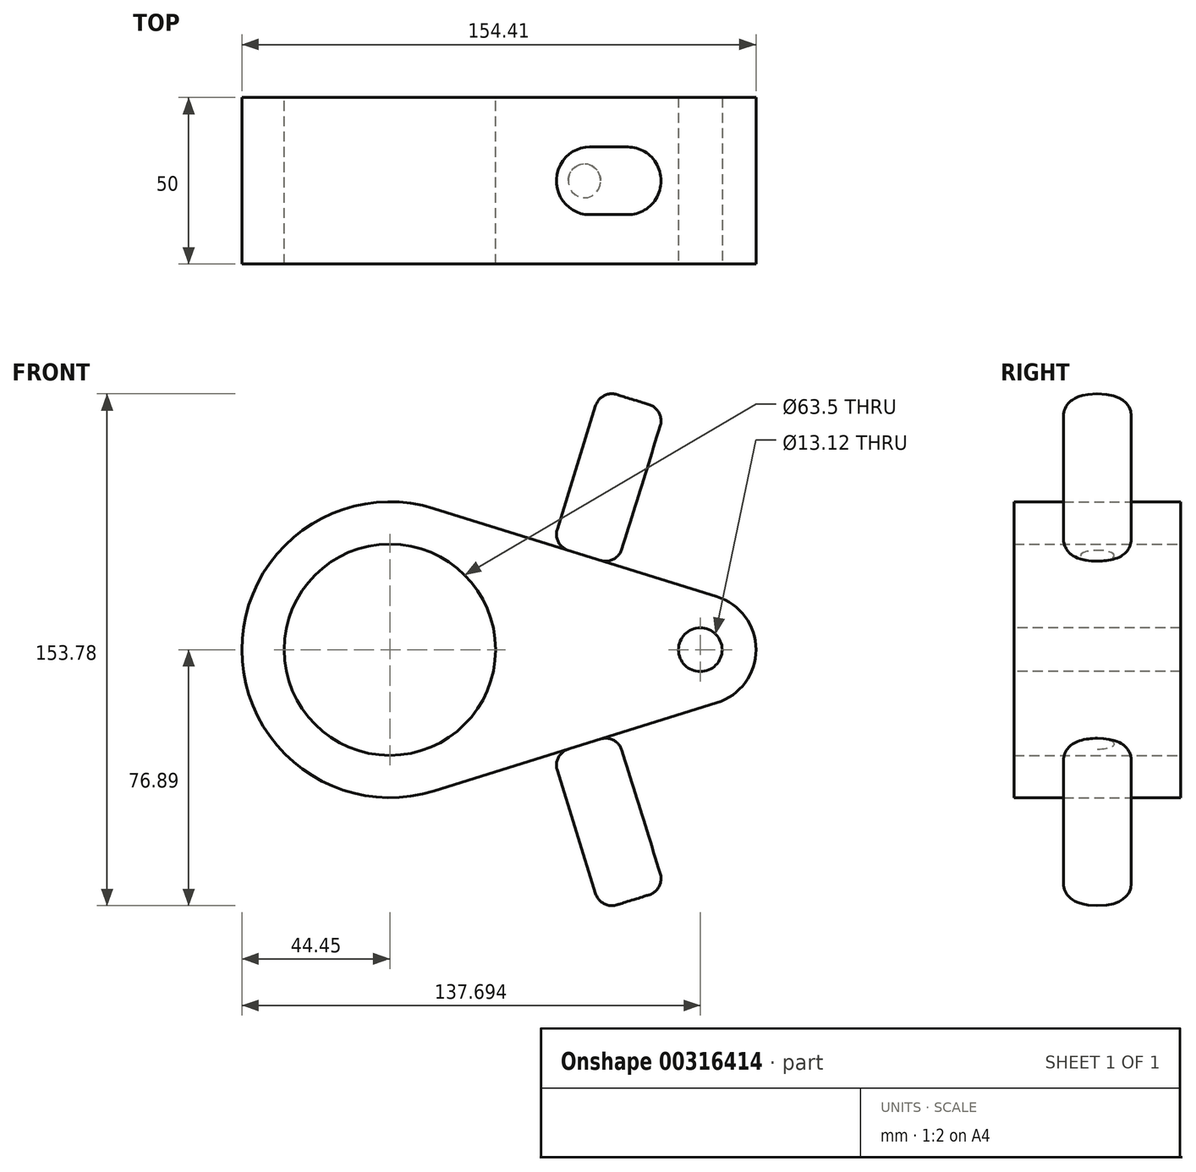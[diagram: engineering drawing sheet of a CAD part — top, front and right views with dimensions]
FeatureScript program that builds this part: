
annotation { "Feature Type Name" : "Feature", "Feature Type Description" : "" }
export const myFeature = defineFeature(function(context is Context, id is Id, definition is map)
    precondition{}
    {
        {
            var Q0;
            Q0=qCreatedBy(makeId("Front.planeOp"),FACE);
            var sketch = newSketch(context, id + "F0", { "sketchPlane" : qUnion([Q0])});
            skCircle(sketch, "E0", {"center": v(0, 0) * mm, "radius": 44.45 * mm});
            skCircle(sketch, "E1", {"center": v(93.24, 0) * mm, "radius": 16.72 * mm});
            skLineSegment(sketch, "E2", {"start": v(13.22, 42.44) * mm, "end": v(98.22, 15.96) * mm});
            skLineSegment(sketch, "E3", {"start": v(13.22, -42.44) * mm, "end": v(98.22, -15.96) * mm});
            skCircle(sketch, "E4", {"center": v(0, 0) * mm, "radius": 31.75 * mm});
            skSolve(sketch);
        }
        {
            var Q0;
            Q0 = qSketchRegion(id + "F0", true);
            extrude(context, id + "F1", {"entities" : qUnion([Q0]), "depth" : 50 * mm});
        }
        {
            var Q0;
            Q0=makeQuery(id+"F1.opExtrude","SWEPT_FACE",FACE,{"disambiguationData":[OSD([sQuery(id+"F0.wireOp",EDGE,"E2")])]});
            var sketch = newSketch(context, id + "F2", { "sketchPlane" : qUnion([Q0])});
            skCircle(sketch, "E5", {"center": v(47.38, -25) * mm, "radius": 10.16 * mm});
            skPoint(sketch, "E5.centerSnap0", {"position": v(89.03, -25) * mm});
            skSolve(sketch);
        }
        {
            var Q0;
            Q0 = qSketchRegion(id + "F2", true);
            extrude(context, id + "F3", {"entities" : qUnion([Q0]), "depth" : 49.02 * mm});
        }
        {
            var Q0;
            Q0=makeQuery(id+"F3.opExtrude","CAP_EDGE",EDGE,{"disambiguationData":[OSD([sQuery(id+"F2.wireOp",EDGE,"E5")])],"isStart":false});
            var Q1;
            Q1=makeQuery(id+"F3.opExtrude","CAP_EDGE",EDGE,{"disambiguationData":[OSD([sQuery(id+"F2.wireOp",EDGE,"E5")])],"isStart":true});
            fillet(context, id + "F4", {"entities" : qUnion([Q0, Q1]), "radius" : 5.08 * mm, "tangentPropagation" : true, "allowEdgeOverflow" : false});
        }
        {
            var Q0;
            Q0=makeQuery(id+"F1.opExtrude","CAP_FACE",FACE,{"disambiguationData":[OSD([sQuery(id+"F0.wireOp",EDGE,"E0"),sQuery(id+"F0.wireOp",EDGE,"E1"),sQuery(id+"F0.wireOp",EDGE,"E2"),sQuery(id+"F0.wireOp",EDGE,"E3"),sQuery(id+"F0.wireOp",EDGE,"E4")])],"isStart":false});
            var sketch = newSketch(context, id + "F5", { "sketchPlane" : qUnion([Q0])});
            skCircle(sketch, "E6", {"center": v(93.24, 0) * mm, "radius": 6.56 * mm});
            skSolve(sketch);
        }
        {
            var Q0;
            Q0=makeQuery(id+"F5.imprint","IMPRINT",FACE,{"disambiguationData":[TD([[makeQuery(id+"F5.imprint","IMPRINT",EDGE,{"derivedFrom":sQuery(id+"F5.wireOp",EDGE,"E6")}),1.0]])]});
            extrude(context, id + "F6", {"entities" : qUnion([Q0]), "operationType" : NewBodyOperationType.REMOVE, "endBound" : BoundingType.THROUGH_ALL, "oppositeDirection" : true, "depth" : 25.4 * mm});
        }
        {
            var Q0;
            Q0=makeQuery(id+"F3.opExtrude","SWEPT_BODY",BODY,{"disambiguationData":[OSD([sQuery(id+"F2.wireOp",EDGE,"E5")])]});
            var Q1;
            Q1=qCreatedBy(makeId("Top.planeOp"),FACE);
            mirror(context, id + "F7", {"operationType" : NewBodyOperationType.ADD, "entities" : qUnion([Q0]), "mirrorPlane" : qUnion([Q1])});
        }
    });
